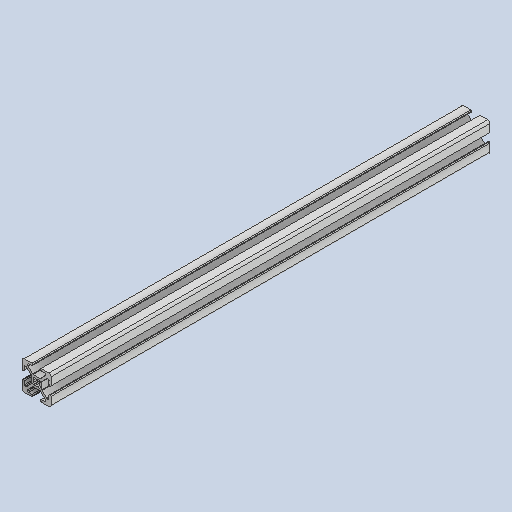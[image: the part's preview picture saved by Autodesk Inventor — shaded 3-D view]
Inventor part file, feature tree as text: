
AUTODESK INVENTOR PART (.ipt)
format: ipt  version: 2022 (Build 260153000, 153)  size: 296,960 bytes
history: native  units: in
note: dims shown in document units (in); Inventor stores cm internally (conversion verified against a paired STEP export)
features: other x3, sketch x1
ambient origin geometry x8: Origin, YZ Plane, XZ Plane, XY Plane, X Axis, Y Axis, Z Axis, Center Point
bodies: Solid1 (feature_tree)
feature tree (4):
  other  "20x20x301.4 T Slot Extrusion Bar_MIR.ipt"
  other  "Solid1::20x20x301.4 T Slot Extrusion Bar_MIR.ipt"
  other  "TaggingFeature1"
  sketch  "Sketch_1"  dims[d0=0.3937in]
